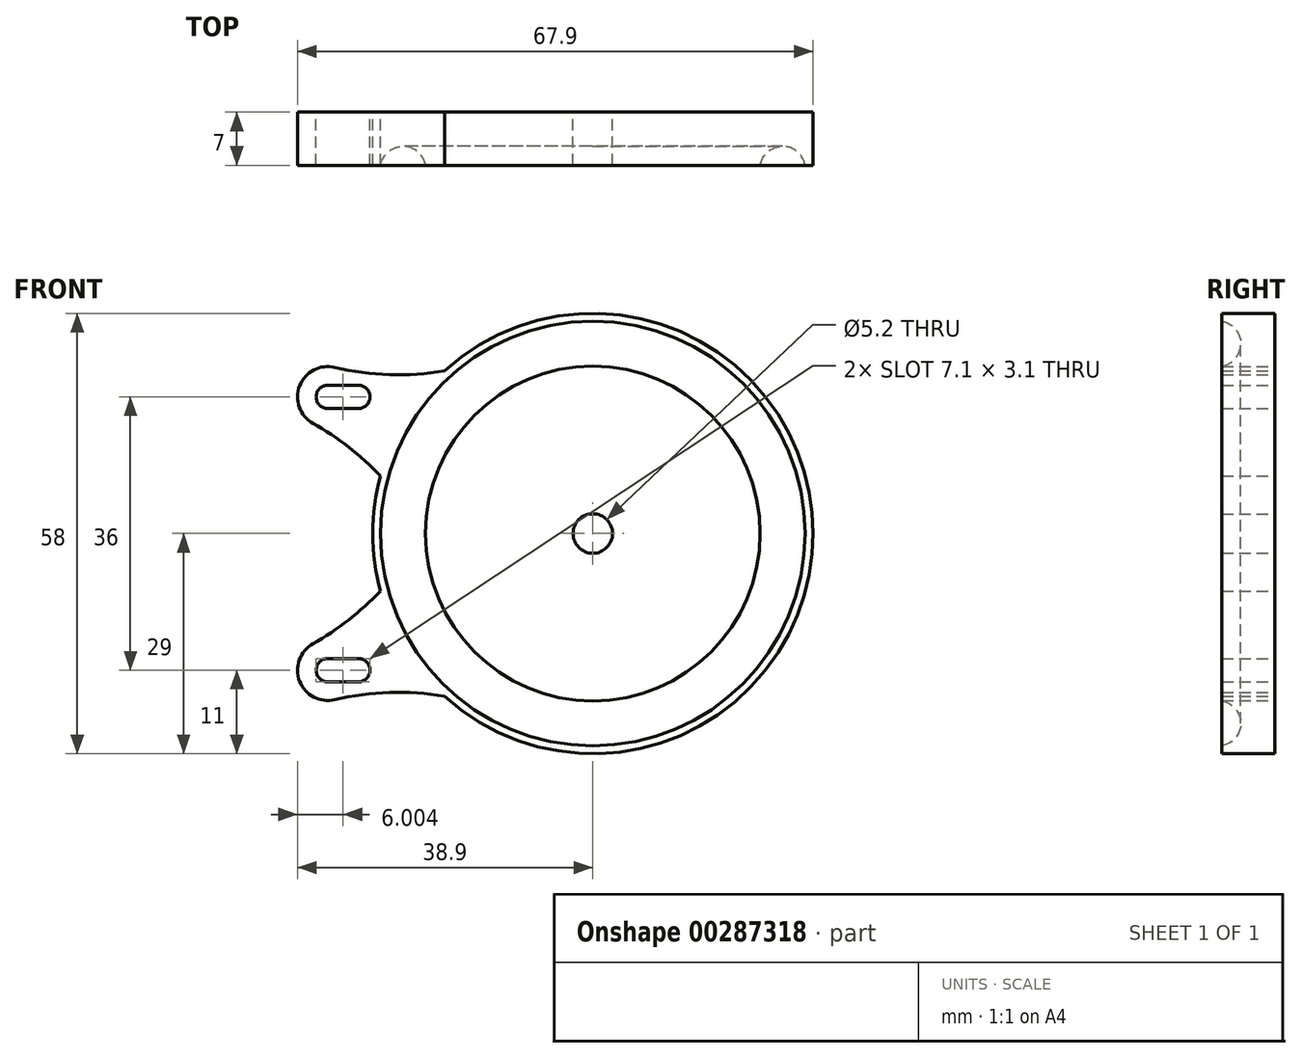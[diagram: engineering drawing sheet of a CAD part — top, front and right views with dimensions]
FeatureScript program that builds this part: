
annotation { "Feature Type Name" : "Feature", "Feature Type Description" : "" }
export const myFeature = defineFeature(function(context is Context, id is Id, definition is map)
    precondition{}
    {
        {
            var Q0;
            Q0=qCreatedBy(makeId("Front.planeOp"),FACE);
            var sketch = newSketch(context, id + "F0", { "sketchPlane" : qUnion([Q0])});
            skCircle(sketch, "E0", {"center": v(0, 0) * mm, "radius": 29 * mm});
            skCircle(sketch, "E1", {"center": v(0, 0) * mm, "radius": 2.6 * mm});
            skArc(sketch, "E2", {"start": v(-33.97, 21.9) * mm, "mid": v(-38.62, 19.47) * mm, "end": v(-36.88, 14.53) * mm});
            skArc(sketch, "E3", {"start": v(-33.97, 21.9) * mm, "mid": v(-26.78, 20.93) * mm, "end": v(-19.55, 21.42) * mm});
            skArc(sketch, "E4", {"start": v(-27.99, 7.59) * mm, "mid": v(-32.18, 11.38) * mm, "end": v(-36.88, 14.53) * mm});
            skArc(sketch, "E5", {"start": v(-34.9, 19.55) * mm, "mid": v(-36.45, 18) * mm, "end": v(-34.9, 16.45) * mm});
            skArc(sketch, "E6", {"start": v(-30.9, 16.45) * mm, "mid": v(-29.35, 18) * mm, "end": v(-30.9, 19.55) * mm});
            skLineSegment(sketch, "E7", {"start": v(-30.9, 19.55) * mm, "end": v(-34.9, 19.55) * mm});
            skLineSegment(sketch, "E8", {"start": v(-30.9, 16.45) * mm, "end": v(-34.9, 16.45) * mm});
            skLineSegment(sketch, "E9.MirrorCS", {"start": v(-30.9, -16.45) * mm, "end": v(-34.9, -16.45) * mm});
            skArc(sketch, "E10.MirrorCS", {"start": v(-33.97, -21.9) * mm, "mid": v(-26.78, -20.93) * mm, "end": v(-19.55, -21.42) * mm});
            skLineSegment(sketch, "E11.MirrorCS", {"start": v(-30.9, -19.55) * mm, "end": v(-34.9, -19.55) * mm});
            skArc(sketch, "E12.MirrorCS", {"start": v(-27.99, -7.59) * mm, "mid": v(-32.18, -11.38) * mm, "end": v(-36.88, -14.53) * mm});
            skArc(sketch, "E13.MirrorCS", {"start": v(-34.9, -19.55) * mm, "mid": v(-36.45, -18) * mm, "end": v(-34.9, -16.45) * mm});
            skArc(sketch, "E14.MirrorCS", {"start": v(-33.97, -21.9) * mm, "mid": v(-38.62, -19.47) * mm, "end": v(-36.88, -14.53) * mm});
            skArc(sketch, "E15.MirrorCS", {"start": v(-30.9, -16.45) * mm, "mid": v(-29.35, -18) * mm, "end": v(-30.9, -19.55) * mm});
            skSolve(sketch);
        }
        {
            var Q0;
            Q0=makeQuery(id+"F0.imprint","IMPRINT",FACE,{"disambiguationData":[TD([[makeQuery(id+"F0.imprint","IMPRINT",EDGE,{"derivedFrom":sQuery(id+"F0.wireOp",EDGE,"E0")}),1.0]])]});
            var Q1;
            {var subQ0=sQuery(id+"F0.wireOp",EDGE,"E3");Q1=makeQuery(id+"F0.imprint","IMPRINT",FACE,{"disambiguationData":[TD([[makeQuery(id+"F0.imprint","IMPRINT",EDGE,{"derivedFrom":subQ0}),-1.0]])]});}
            var Q2;
            {var subQ0=sQuery(id+"F0.wireOp",EDGE,"E2");var subQ1=makeQuery(id+"F0.imprint","INTERSECT",VERTEX,{"derivedFrom":[subQ0,sQuery(id+"F0.wireOp",EDGE,"E3")]});Q2=makeQuery(id+"F0.imprint","IMPRINT",FACE,{"disambiguationData":[TD([[makeQuery(id+"F0.imprint","IMPRINT",EDGE,{"disambiguationData":[TD([[subQ1,-1.0]])],"derivedFrom":subQ0}),1.0]])]});}
            var Q3;
            {var subQ0=sQuery(id+"F0.wireOp",EDGE,"a499c0e8-2c50-40d2-bf47-fcc7598a5a3d0.MirrorCS");Q3=makeQuery(id+"F0.imprint","IMPRINT",FACE,{"disambiguationData":[TD([[makeQuery(id+"F0.imprint","IMPRINT",EDGE,{"derivedFrom":subQ0}),1.0]])]});}
            var Q4;
            {var subQ0=sQuery(id+"F0.wireOp",EDGE,"40a46fe1-b053-4aaf-b6c9-ff617f6dc9b50.MirrorC");var subQ1=makeQuery(id+"F0.imprint","INTERSECT",VERTEX,{"derivedFrom":[subQ0,sQuery(id+"F0.wireOp",EDGE,"a499c0e8-2c50-40d2-bf47-fcc7598a5a3d0.MirrorCS")]});Q4=makeQuery(id+"F0.imprint","IMPRINT",FACE,{"disambiguationData":[TD([[makeQuery(id+"F0.imprint","IMPRINT",EDGE,{"disambiguationData":[TD([[subQ1,1.0]])],"derivedFrom":subQ0}),-1.0]])]});}
            var Q5;
            Q5=makeQuery(id+"F0.imprint","IMPRINT",FACE,{"disambiguationData":[TD([[makeQuery(id+"F0.imprint","IMPRINT",EDGE,{"derivedFrom":sQuery(id+"F0.wireOp",EDGE,"E9.MirrorCS")}),-1.0]])]});
            extrude(context, id + "F1", {"entities" : qUnion([Q0, Q1, Q2, Q3, Q4, Q5]), "offsetDistance" : 25 * mm, "depth" : 7 * mm});
        }
        {
            var Q0;
            Q0=qCreatedBy(makeId("Right.planeOp"),FACE);
            var sketch = newSketch(context, id + "F2", { "sketchPlane" : qUnion([Q0])});
            skCircle(sketch, "E16", {"center": v(-7.5, 25) * mm, "radius": 3 * mm});
            skSolve(sketch);
        }
        {
            var Q0;
            Q0=makeQuery(id+"F2.imprint","IMPRINT",FACE,{"disambiguationData":[TD([[makeQuery(id+"F2.imprint","IMPRINT",EDGE,{"derivedFrom":sQuery(id+"F2.wireOp",EDGE,"E16")}),1.0]])]});
            var Q1;
            Q1=sQuery(id+"F0.wireOp",EDGE,"E0");
            revolve(context, id + "F3", {"operationType" : NewBodyOperationType.REMOVE, "entities" : qUnion([Q0]), "axis" : qUnion([Q1]), "revolveType" : RevolveType.FULL, "oppositeDirection" : true});
        }
    });
